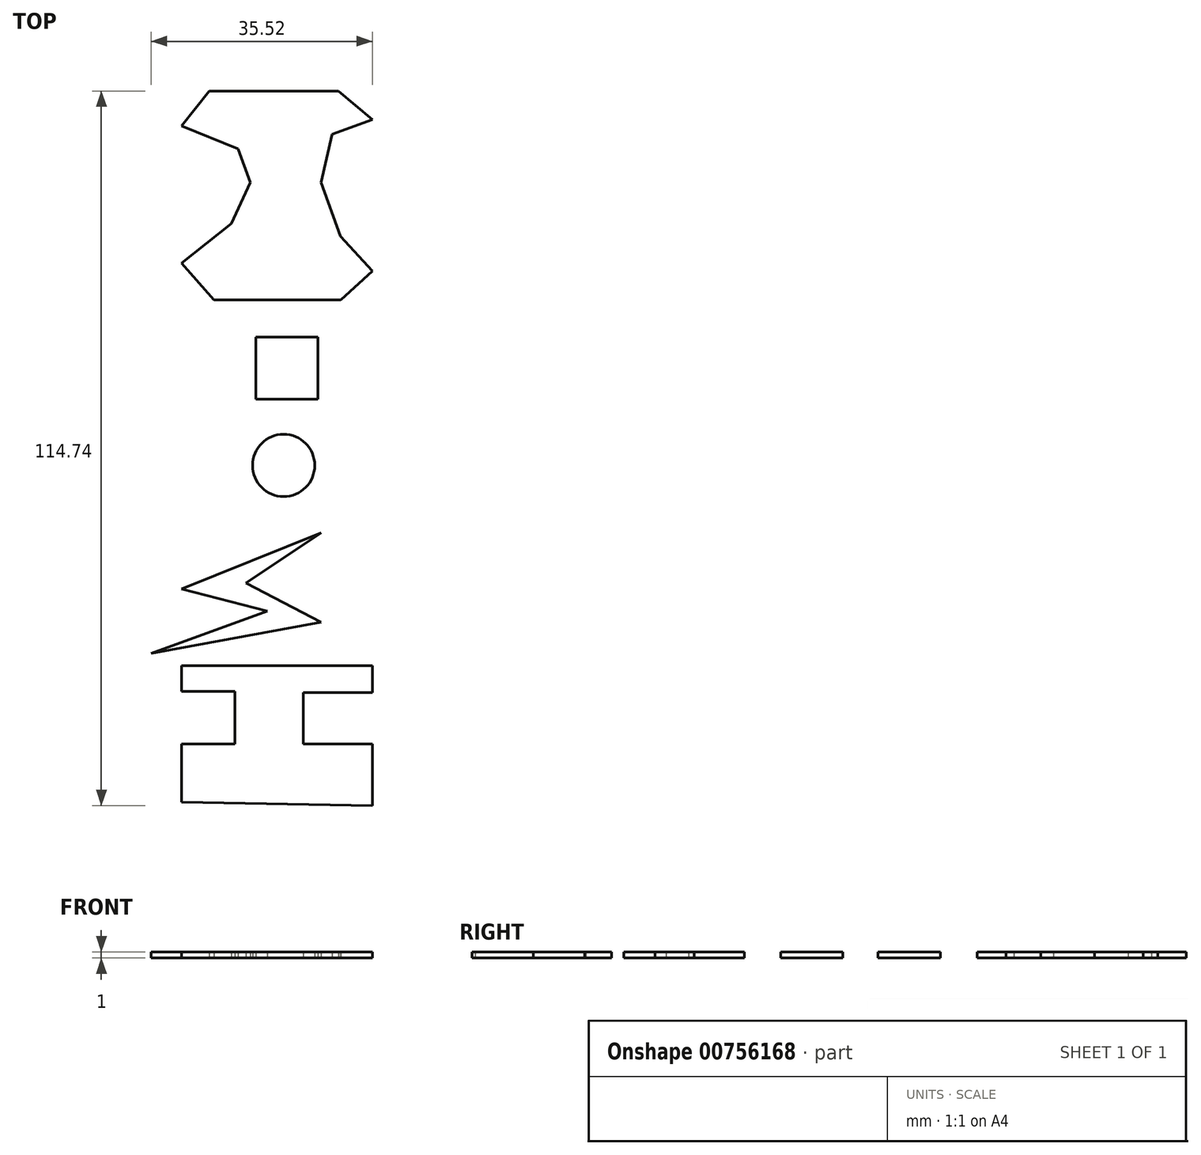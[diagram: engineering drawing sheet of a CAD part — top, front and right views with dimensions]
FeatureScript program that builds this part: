
annotation { "Feature Type Name" : "Feature", "Feature Type Description" : "" }
export const myFeature = defineFeature(function(context is Context, id is Id, definition is map)
    precondition{}
    {
        {
            var Q0;
            Q0=qCreatedBy(makeId("Top.planeOp"),FACE);
            var sketch = newSketch(context, id + "F0", { "sketchPlane" : qUnion([Q0])});
            skLineSegment(sketch, "E0.bottom", {"start": v(-4.48, 20.63) * mm, "end": v(5.52, 20.63) * mm});
            skLineSegment(sketch, "E0.top", {"start": v(-4.48, 10.63) * mm, "end": v(5.52, 10.63) * mm});
            skLineSegment(sketch, "E0.left", {"start": v(-4.48, 20.63) * mm, "end": v(-4.48, 10.63) * mm});
            skLineSegment(sketch, "E0.right", {"start": v(5.52, 20.63) * mm, "end": v(5.52, 10.63) * mm});
            skCircle(sketch, "E1", {"center": v(0, 0) * mm, "radius": 5 * mm});
            skLineSegment(sketch, "E2", {"start": v(-16.43, -19.81) * mm, "end": v(6, -10.84) * mm});
            skLineSegment(sketch, "E3", {"start": v(6, -10.84) * mm, "end": v(-6.02, -18.91) * mm});
            skLineSegment(sketch, "E4", {"start": v(-6.02, -18.91) * mm, "end": v(6, -25.2) * mm});
            skLineSegment(sketch, "E5", {"start": v(6, -25.2) * mm, "end": v(-21.27, -30.22) * mm});
            skLineSegment(sketch, "E6", {"start": v(-21.27, -30.22) * mm, "end": v(-2.61, -23.4) * mm});
            skLineSegment(sketch, "E7", {"start": v(-2.61, -23.4) * mm, "end": v(-16.43, -19.81) * mm});
            skLineSegment(sketch, "E8", {"start": v(-16.43, -54.08) * mm, "end": v(-16.43, -44.75) * mm});
            skLineSegment(sketch, "E9", {"start": v(-16.43, -44.75) * mm, "end": v(-7.82, -44.75) * mm});
            skLineSegment(sketch, "E10", {"start": v(-7.82, -44.75) * mm, "end": v(-7.82, -36.32) * mm});
            skLineSegment(sketch, "E11", {"start": v(-7.82, -36.32) * mm, "end": v(-16.43, -36.32) * mm});
            skLineSegment(sketch, "E12", {"start": v(-16.43, -36.32) * mm, "end": v(-16.43, -32.19) * mm});
            skLineSegment(sketch, "E13", {"start": v(-16.43, -32.19) * mm, "end": v(14.25, -32.19) * mm});
            skLineSegment(sketch, "E14", {"start": v(14.25, -32.19) * mm, "end": v(14.25, -36.5) * mm});
            skLineSegment(sketch, "E15", {"start": v(14.25, -36.5) * mm, "end": v(3.13, -36.5) * mm});
            skLineSegment(sketch, "E16", {"start": v(3.13, -36.5) * mm, "end": v(3.13, -44.75) * mm});
            skLineSegment(sketch, "E17", {"start": v(3.13, -44.75) * mm, "end": v(14.25, -44.75) * mm});
            skLineSegment(sketch, "E18", {"start": v(14.25, -44.75) * mm, "end": v(14.25, -54.61) * mm});
            skLineSegment(sketch, "E19", {"start": v(14.25, -54.61) * mm, "end": v(-16.43, -54.08) * mm});
            skLineSegment(sketch, "E20", {"start": v(-16.43, 32.48) * mm, "end": v(-8.42, 38.82) * mm});
            skLineSegment(sketch, "E21", {"start": v(-8.42, 38.82) * mm, "end": v(-5.37, 45.42) * mm});
            skLineSegment(sketch, "E22", {"start": v(-5.37, 45.42) * mm, "end": v(-7.34, 50.81) * mm});
            skLineSegment(sketch, "E23", {"start": v(-7.34, 50.81) * mm, "end": v(-16.43, 54.55) * mm});
            skLineSegment(sketch, "E24", {"start": v(-16.43, 54.55) * mm, "end": v(-11.97, 60.13) * mm});
            skLineSegment(sketch, "E25", {"start": v(-11.97, 60.13) * mm, "end": v(8.83, 60.13) * mm});
            skLineSegment(sketch, "E26", {"start": v(8.83, 60.13) * mm, "end": v(14.25, 55.56) * mm});
            skLineSegment(sketch, "E27", {"start": v(14.25, 55.56) * mm, "end": v(7.8, 53.2) * mm});
            skLineSegment(sketch, "E28", {"start": v(7.8, 53.2) * mm, "end": v(6, 45.42) * mm});
            skLineSegment(sketch, "E29", {"start": v(6, 45.42) * mm, "end": v(9.14, 36.8) * mm});
            skLineSegment(sketch, "E30", {"start": v(9.14, 36.8) * mm, "end": v(14.25, 31.2) * mm});
            skLineSegment(sketch, "E31", {"start": v(14.25, 31.2) * mm, "end": v(9.16, 26.57) * mm});
            skLineSegment(sketch, "E32", {"start": v(9.16, 26.57) * mm, "end": v(-11.16, 26.57) * mm});
            skLineSegment(sketch, "E33", {"start": v(-11.16, 26.57) * mm, "end": v(-16.43, 32.48) * mm});
            skSolve(sketch);
        }
        {
            var Q0;
            Q0 = qSketchRegion(id + "F0", true);
            extrude(context, id + "F1", {"entities" : qUnion([Q0]), "depth" : 1 * mm, "offsetDistance" : 25 * mm});
        }
    });
